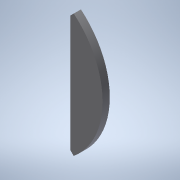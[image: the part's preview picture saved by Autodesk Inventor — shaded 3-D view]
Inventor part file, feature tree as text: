
AUTODESK INVENTOR PART (.ipt)
format: ipt  version: 2021.3 (Build 253353010, 353A)  size: 97,792 bytes
history: native  units: mm
features: extrude x1, sketch x1
ambient origin geometry x8: Origin, YZ Plane, XZ Plane, XY Plane, X Axis, Y Axis, Z Axis, Center Point
bodies: Solid1 (feature_tree)
feature tree (2):
  extrude  "Extrusion1"  Depth=3.0mm
  sketch  "Sketch1"  dims[d0=48.5mm d1=2.069mm d2=45.0deg d3=2.069mm d4=45.0deg d6=67.0mm d7=20.0mm d8=3.0mm d9=0.0mm]
